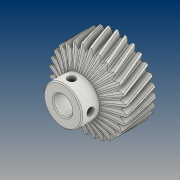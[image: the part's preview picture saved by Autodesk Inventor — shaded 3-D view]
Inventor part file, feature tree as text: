
AUTODESK INVENTOR PART (.ipt)
format: ipt  version: 2021 (Build 250183000, 183)  size: 971,264 bytes
history: native  units: mm (DEFAULTED — no unit token found)
features: sketch x6, extrude x5, plane x4, other x4, chamfer x2, pattern_circular x1, loft x1, projected_geometry x1
ambient origin geometry x8: Origin, YZ Plane, XZ Plane, XY Plane, X Axis, Y Axis, Z Axis, Center Point
bodies: Solid1 (feature_tree)
feature tree (24):
  extrude  "Extrusion1"  Depth=15.0mm TaperAngle=0.0deg
  plane  "Work Plane2"
  plane  "Work Plane8"
  plane  "Work Plane9"
  other  "Spur Gear"
  sketch  "Sketch3"  dims[d16=45.0mm d17=0.0mm d34=1.121997mm]
  extrude  "Extrusion2"  Depth=10.0mm TaperAngle=0.0deg
  extrude  "Extrusion3"  Depth=1.121997mm TaperAngle=0.0deg
  chamfer  "Chamfer1"  Distance=45.0mm
  chamfer  "Chamfer2"  [1 undecoded]
  extrude  "Extrusion4"  Depth=9.6mm
  pattern_circular  "Circular Pattern1"  [2 undecoded]
  plane  "Work Plane11"
  loft  "Loft1"
  extrude  "Extrusion5"  Depth=13.0mm TaperAngle=0.0deg
  sketch  "Sketch1"  dims[d0=39.395974mm d1=15.0mm d2=0.0mm]
  sketch  "Sketch2"  dims[d3=37.246222mm d4=10.0mm d5=0.0mm]
  other  "Srf1"
  sketch  "Sketch4"  dims[d39=0.0mm]
  projected_geometry  "Projected Loop1"
  sketch  "Sketch5"  dims[d41=0.0mm]
  other  "Edges1"
  sketch  "Sketch6"  dims[d43=45.0mm d46=45.0mm d47=0.0mm d48=0.0mm d49=9.6mm d50=5.0mm d51=69.5mm d52=0.0mm d53=13.0mm d54=0.0mm d55=0.5mm d56=2.0mm d57=45.0deg d58=0.5mm d59=2.0mm d60=45.0deg d62=4.0mm d63=3.8mm d64=10.0mm d65=0.0mm d66=20.0mm d67=90.0deg d69=4.0mm d70=0.0mm d71=90.0deg d72=0.0mm d73=90.0deg d74=46.25mm d75=0.0mm]
  other  "Pitch Diameter"
note: 3 required parameter values undecoded (feature->parameter linkage not recoverable at this tier; creation-order binding heuristic only, values carry confidence <= 0.55)
